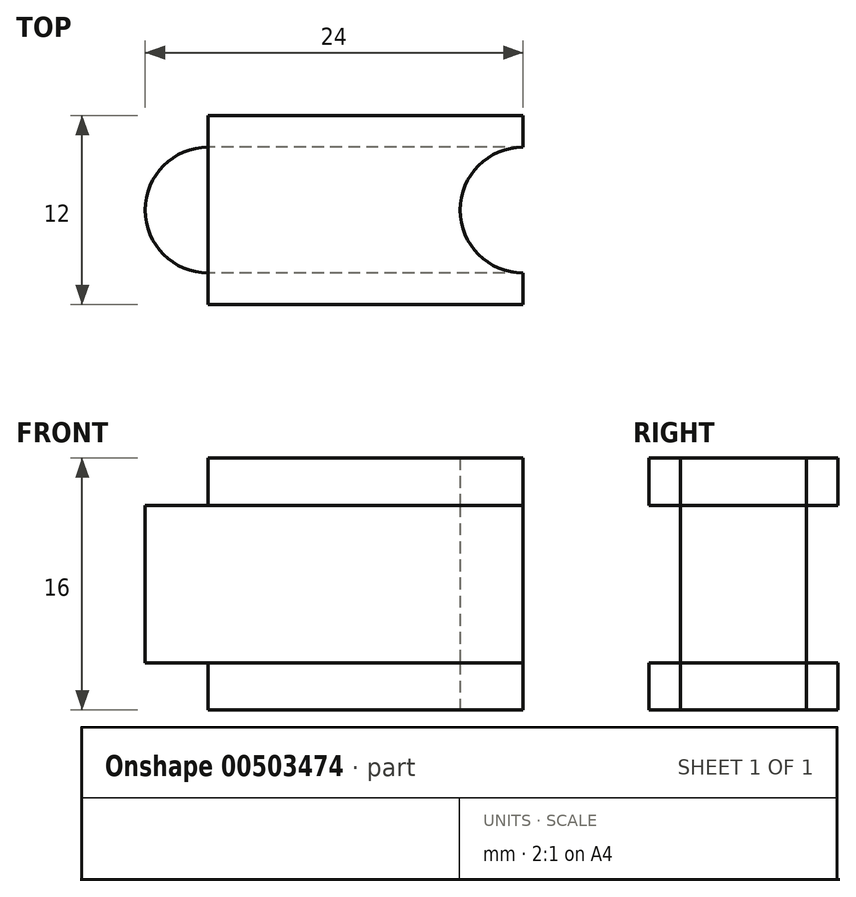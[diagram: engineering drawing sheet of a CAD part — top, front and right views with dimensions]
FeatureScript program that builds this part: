
annotation { "Feature Type Name" : "Feature", "Feature Type Description" : "" }
export const myFeature = defineFeature(function(context is Context, id is Id, definition is map)
    precondition{}
    {
        {
            var Q0;
            Q0=qCreatedBy(makeId("Top.planeOp"),FACE);
            var sketch = newSketch(context, id + "F0", { "sketchPlane" : qUnion([Q0])});
            skCircle(sketch, "E0", {"center": v(0, 0) * mm, "radius": 4 * mm});
            skLineSegment(sketch, "E1", {"start": v(0, 0) * mm, "end": v(20, 0) * mm});
            skLineSegment(sketch, "E2", {"start": v(20, 4) * mm, "end": v(0, 4) * mm});
            skLineSegment(sketch, "E3", {"start": v(20, -4) * mm, "end": v(0, -4) * mm});
            skArc(sketch, "E4", {"start": v(20, 4) * mm, "mid": v(16, 0) * mm, "end": v(20, -4) * mm});
            skSolve(sketch);
        }
        {
            var Q0;
            Q0 = qSketchRegion(id + "F0", true);
            extrude(context, id + "F1", {"entities" : qUnion([Q0]), "endBound" : BoundingType.SYMMETRIC, "depth" : 10 * mm});
        }
        {
            var Q0;
            Q0=qCreatedBy(makeId("Top.planeOp"),FACE);
            var sketch = newSketch(context, id + "F2", { "sketchPlane" : qUnion([Q0])});
            skLineSegment(sketch, "E5", {"start": v(0, 0) * mm, "end": v(20, 0) * mm});
            skArc(sketch, "E6", {"start": v(20, 4) * mm, "mid": v(16, 0) * mm, "end": v(20, -4) * mm});
            skLineSegment(sketch, "E7", {"start": v(0, 0) * mm, "end": v(0, 6) * mm});
            skLineSegment(sketch, "E8", {"start": v(0, 6) * mm, "end": v(20, 6) * mm});
            skLineSegment(sketch, "E9", {"start": v(20, 6) * mm, "end": v(20, 4) * mm});
            skLineSegment(sketch, "E10", {"start": v(0, 0) * mm, "end": v(0, -6) * mm});
            skLineSegment(sketch, "E11", {"start": v(0, -6) * mm, "end": v(20, -6) * mm});
            skLineSegment(sketch, "E12", {"start": v(20, -6) * mm, "end": v(20, -4) * mm});
            skSolve(sketch);
        }
        {
            var Q0;
            Q0 = qSketchRegion(id + "F2", true);
            extrude(context, id + "F3", {"entities" : qUnion([Q0]), "endBound" : BoundingType.SYMMETRIC, "depth" : 3 * mm});
        }
        {
            var Q0;
            Q0=makeQuery(id+"F3.opExtrude","SWEPT_BODY",BODY,{"disambiguationData":[OSD([sQuery(id+"F2.wireOp",EDGE,"E6"),sQuery(id+"F2.wireOp",EDGE,"E7"),sQuery(id+"F2.wireOp",EDGE,"E8"),sQuery(id+"F2.wireOp",EDGE,"E9"),sQuery(id+"F2.wireOp",EDGE,"E10"),sQuery(id+"F2.wireOp",EDGE,"E11"),sQuery(id+"F2.wireOp",EDGE,"E12")])]});
            transform(context, id + "F4", {"entities" : qUnion([Q0]), "transformType" : TransformType.TRANSLATION_3D, "dx" : 0 * mm, "dy" : 0 * mm, "dz" : 6.5 * mm, "makeCopy" : true});
        }
        {
            var Q0;
            Q0=makeQuery(id+"F3.opExtrude","SWEPT_BODY",BODY,{"disambiguationData":[OSD([sQuery(id+"F2.wireOp",EDGE,"E6"),sQuery(id+"F2.wireOp",EDGE,"E7"),sQuery(id+"F2.wireOp",EDGE,"E8"),sQuery(id+"F2.wireOp",EDGE,"E9"),sQuery(id+"F2.wireOp",EDGE,"E10"),sQuery(id+"F2.wireOp",EDGE,"E11"),sQuery(id+"F2.wireOp",EDGE,"E12")])]});
            transform(context, id + "F5", {"entities" : qUnion([Q0]), "transformType" : TransformType.TRANSLATION_3D, "dx" : 0 * mm, "dy" : 0 * mm, "dz" : -6.5 * mm, "makeCopy" : false});
        }
    });
